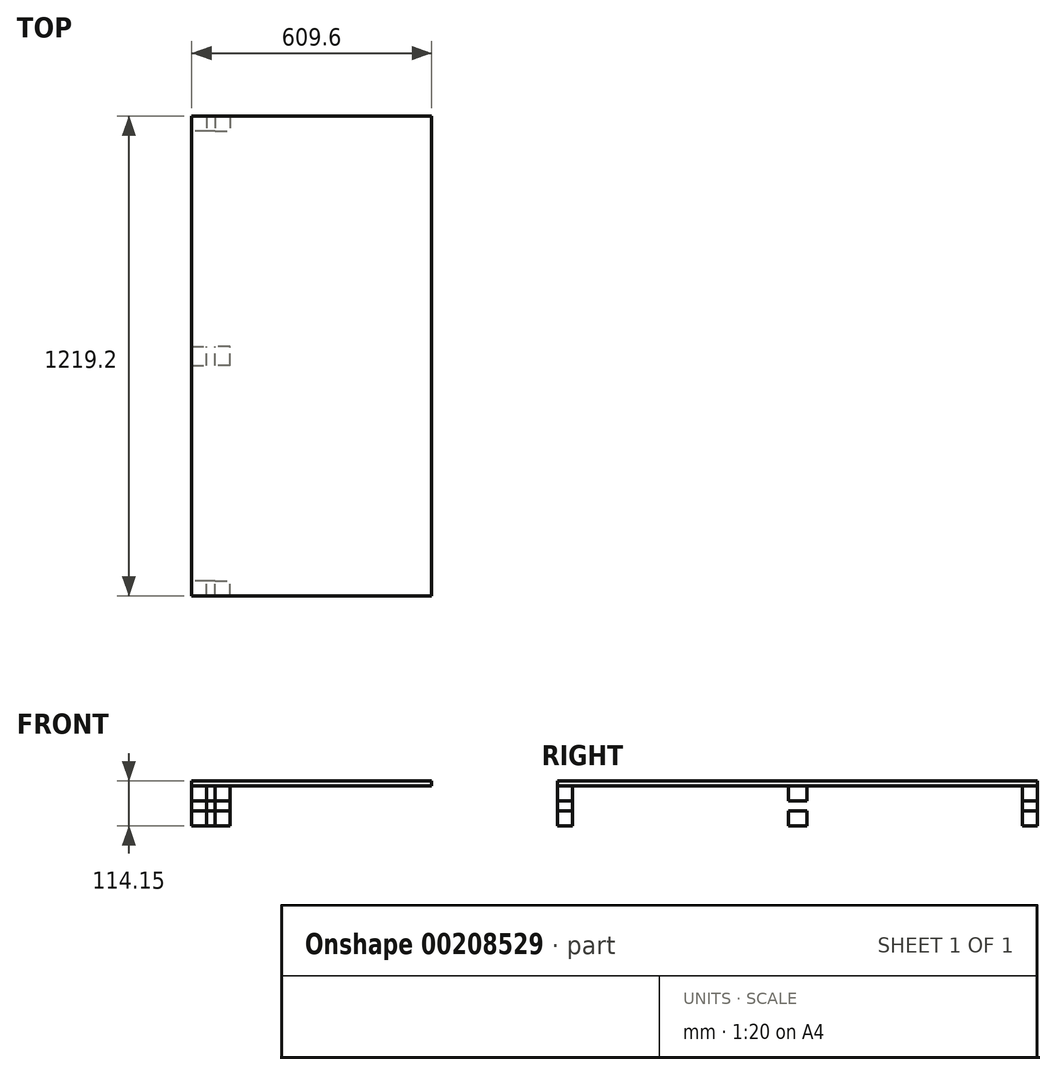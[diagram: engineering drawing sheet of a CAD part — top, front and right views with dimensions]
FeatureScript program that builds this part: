
annotation { "Feature Type Name" : "Feature", "Feature Type Description" : "" }
export const myFeature = defineFeature(function(context is Context, id is Id, definition is map)
    precondition{}
    {
        {
            assignVariable(context, id + "F0", {"name" : "ExtrudeSize", "anyValue" : 1});
        }
        {
            assignVariable(context, id + "F1", {"name" : "ProfileWidth", "anyValue" : [1, 1.5, 1.5][getVariable(context, 'ExtrudeSize')]});
        }
        {
            assignVariable(context, id + "F2", {"name" : "ProfileHeight", "anyValue" : [1, 1.5, 3][getVariable(context, 'ExtrudeSize')]});
        }
        {
            assignVariable(context, id + "F3", {"name" : "Length", "anyValue" : 48});
        }
        {
            assignVariable(context, id + "F4", {"name" : "Width", "anyValue" : 24});
        }
        {
            assignVariable(context, id + "F5", {"name" : "Height", "anyValue" : 34});
        }
        {
            assignVariable(context, id + "F6", {"name" : "AcrylicThickness", "anyValue" : .5});
        }
        {
            var Q0;
            Q0=qCreatedBy(makeId("Front.planeOp"),FACE);
            var sketch = newSketch(context, id + "F7", { "sketchPlane" : qUnion([Q0])});
            skLineSegment(sketch, "E0.bottom", {"start": v(0, 0) * mm, "end": v(38.1, 0) * mm});
            skLineSegment(sketch, "E0.top", {"start": v(0, 38.1) * mm, "end": v(38.1, 38.1) * mm});
            skLineSegment(sketch, "E0.left", {"start": v(0, 0) * mm, "end": v(0, 38.1) * mm});
            skLineSegment(sketch, "E0.right", {"start": v(38.1, 0) * mm, "end": v(38.1, 38.1) * mm});
            skSolve(sketch);
        }
        {
            var Q0;
            Q0 = qSketchRegion(id + "F7", true);
            extrude(context, id + "F8", {"entities" : qUnion([Q0]), "depth" : (getVariable(context, 'Length')) * mm, "symmetric" : true});
        }
        {
            var Q0;
            Q0=makeQuery(id+"F8.opExtrude","SWEPT_FACE",FACE,{"disambiguationData":[OSD([sQuery(id+"F7.wireOp",EDGE,"E0.right")])]});
            var sketch = newSketch(context, id + "F9", { "sketchPlane" : qUnion([Q0])});
            skLineSegment(sketch, "E1.bottom", {"start": v(-609.6, 0) * mm, "end": v(-571.5, 0) * mm});
            skLineSegment(sketch, "E1.top", {"start": v(-609.6, 38.1) * mm, "end": v(-571.5, 38.1) * mm});
            skLineSegment(sketch, "E1.left", {"start": v(-609.6, 0) * mm, "end": v(-609.6, 38.1) * mm});
            skLineSegment(sketch, "E1.right", {"start": v(-571.5, 0) * mm, "end": v(-571.5, 38.1) * mm});
            skSolve(sketch);
        }
        {
            var Q0;
            Q0=makeQuery(id+"F9.imprint","IMPRINT",FACE,{"disambiguationData":[TD([[makeQuery(id+"F9.imprint","IMPRINT",EDGE,{"derivedFrom":sQuery(id+"F9.wireOp",EDGE,"E1.bottom")}),1.0]])]});
            extrude(context, id + "F10", {"entities" : qUnion([Q0]), "depth" : ((getVariable(context, 'Width')) - 2 * (getVariable(context, 'ProfileWidth'))) * mm});
        }
        {
            var Q0;
            Q0=makeQuery(id+"F10.opExtrude","SWEPT_BODY",BODY,{"disambiguationData":[OSD([sQuery(id+"F9.wireOp",EDGE,"E1.bottom"),sQuery(id+"F9.wireOp",EDGE,"E1.top"),sQuery(id+"F9.wireOp",EDGE,"E1.left"),sQuery(id+"F9.wireOp",EDGE,"E1.right")])]});
            var Q1;
            Q1=qCreatedBy(makeId("Front.planeOp"),FACE);
            mirror(context, id + "F11", {"entities" : qUnion([Q0]), "mirrorPlane" : qUnion([Q1])});
        }
        {
            var Q0;
            Q0=makeQuery(id+"F10.opExtrude","CAP_FACE",FACE,{"disambiguationData":[OSD([sQuery(id+"F9.wireOp",EDGE,"E1.bottom"),sQuery(id+"F9.wireOp",EDGE,"E1.top"),sQuery(id+"F9.wireOp",EDGE,"E1.left"),sQuery(id+"F9.wireOp",EDGE,"E1.right")])],"isStart":false});
            var Q1;
            Q1=makeQuery(id+"F10.opExtrude","CAP_FACE",FACE,{"disambiguationData":[OSD([sQuery(id+"F9.wireOp",EDGE,"E1.bottom"),sQuery(id+"F9.wireOp",EDGE,"E1.top"),sQuery(id+"F9.wireOp",EDGE,"E1.left"),sQuery(id+"F9.wireOp",EDGE,"E1.right")])],"isStart":true});
            cPlane(context, id + "F12", {"entities" : qUnion([Q0, Q1]), "cplaneType" : CPlaneType.MID_PLANE, "offset" : 25.4 * mm, "width" : 152.4 * mm, "height" : 152.4 * mm});
        }
        {
            var Q0;
            Q0=makeQuery(id+"F8.opExtrude","SWEPT_BODY",BODY,{"disambiguationData":[OSD([sQuery(id+"F7.wireOp",EDGE,"E0.bottom"),sQuery(id+"F7.wireOp",EDGE,"E0.top"),sQuery(id+"F7.wireOp",EDGE,"E0.left"),sQuery(id+"F7.wireOp",EDGE,"E0.right")])]});
            var Q1;
            Q1=qCreatedBy(id+"F12.planeOp",FACE);
            mirror(context, id + "F13", {"entities" : qUnion([Q0]), "mirrorPlane" : qUnion([Q1])});
        }
        {
            var Q0;
            Q0=makeQuery(id+"F8.opExtrude","SWEPT_FACE",FACE,{"disambiguationData":[OSD([sQuery(id+"F7.wireOp",EDGE,"E0.top")])]});
            var sketch = newSketch(context, id + "F14", { "sketchPlane" : qUnion([Q0])});
            skLineSegment(sketch, "E2.bottom", {"start": v(38.1, -609.6) * mm, "end": v(0, -609.6) * mm});
            skLineSegment(sketch, "E2.top", {"start": v(38.1, -571.5) * mm, "end": v(0, -571.5) * mm});
            skLineSegment(sketch, "E2.left", {"start": v(38.1, -609.6) * mm, "end": v(38.1, -571.5) * mm});
            skLineSegment(sketch, "E2.right", {"start": v(0, -609.6) * mm, "end": v(0, -571.5) * mm});
            skSolve(sketch);
        }
        {
            var Q0;
            Q0 = qSketchRegion(id + "F14", true);
            extrude(context, id + "F15", {"entities" : qUnion([Q0]), "depth" : (getVariable(context, 'Height') - ((2 * (getVariable(context, 'ProfileHeight'))) + 5.25 + (getVariable(context, 'AcrylicThickness')))) * mm});
        }
        {
            var Q0;
            Q0=makeQuery(id+"F15.opExtrude","SWEPT_BODY",BODY,{"disambiguationData":[OSD([sQuery(id+"F14.wireOp",EDGE,"E2.bottom"),sQuery(id+"F14.wireOp",EDGE,"E2.top"),sQuery(id+"F14.wireOp",EDGE,"E2.left"),sQuery(id+"F14.wireOp",EDGE,"E2.right")])]});
            var Q1;
            Q1=qCreatedBy(makeId("Front.planeOp"),FACE);
            mirror(context, id + "F16", {"entities" : qUnion([Q0]), "mirrorPlane" : qUnion([Q1])});
        }
        {
            var Q0;
            Q0=makeQuery(id+"F15.opExtrude","SWEPT_BODY",BODY,{"disambiguationData":[OSD([sQuery(id+"F14.wireOp",EDGE,"E2.bottom"),sQuery(id+"F14.wireOp",EDGE,"E2.top"),sQuery(id+"F14.wireOp",EDGE,"E2.left"),sQuery(id+"F14.wireOp",EDGE,"E2.right")])]});
            var Q1;
            Q1=makeQuery(id+"F16.opPattern","COPY",BODY,{"derivedFrom":makeQuery(id+"F15.opExtrude","SWEPT_BODY",BODY,{"disambiguationData":[OSD([sQuery(id+"F14.wireOp",EDGE,"E2.bottom"),sQuery(id+"F14.wireOp",EDGE,"E2.top"),sQuery(id+"F14.wireOp",EDGE,"E2.left"),sQuery(id+"F14.wireOp",EDGE,"E2.right")])]}),"instanceName":"1"});
            var Q2;
            Q2=qCreatedBy(id+"F12.planeOp",FACE);
            mirror(context, id + "F17", {"entities" : qUnion([Q0, Q1]), "mirrorPlane" : qUnion([Q2])});
        }
        {
            var Q0;
            Q0=makeQuery(id+"F16.opPattern","COPY",FACE,{"derivedFrom":makeQuery(id+"F15.opExtrude","CAP_FACE",FACE,{"disambiguationData":[OSD([sQuery(id+"F14.wireOp",EDGE,"E2.bottom"),sQuery(id+"F14.wireOp",EDGE,"E2.top"),sQuery(id+"F14.wireOp",EDGE,"E2.left"),sQuery(id+"F14.wireOp",EDGE,"E2.right")])],"isStart":false}),"instanceName":"1"});
            var Q1;
            Q1=makeQuery(id+"F16.opPattern","COPY",FACE,{"derivedFrom":makeQuery(id+"F15.opExtrude","CAP_FACE",FACE,{"disambiguationData":[OSD([sQuery(id+"F14.wireOp",EDGE,"E2.bottom"),sQuery(id+"F14.wireOp",EDGE,"E2.top"),sQuery(id+"F14.wireOp",EDGE,"E2.left"),sQuery(id+"F14.wireOp",EDGE,"E2.right")])],"isStart":true}),"instanceName":"1"});
            cPlane(context, id + "F18", {"entities" : qUnion([Q0, Q1]), "cplaneType" : CPlaneType.MID_PLANE, "offset" : 25.4 * mm, "width" : 152.4 * mm, "height" : 152.4 * mm});
        }
        {
            var Q0;
            Q0=makeQuery(id+"F8.opExtrude","SWEPT_BODY",BODY,{"disambiguationData":[OSD([sQuery(id+"F7.wireOp",EDGE,"E0.bottom"),sQuery(id+"F7.wireOp",EDGE,"E0.top"),sQuery(id+"F7.wireOp",EDGE,"E0.left"),sQuery(id+"F7.wireOp",EDGE,"E0.right")])]});
            var Q1;
            Q1=makeQuery(id+"F11.opPattern","COPY",BODY,{"derivedFrom":makeQuery(id+"F10.opExtrude","SWEPT_BODY",BODY,{"disambiguationData":[OSD([sQuery(id+"F9.wireOp",EDGE,"E1.bottom"),sQuery(id+"F9.wireOp",EDGE,"E1.top"),sQuery(id+"F9.wireOp",EDGE,"E1.left"),sQuery(id+"F9.wireOp",EDGE,"E1.right")])]}),"instanceName":"1"});
            var Q2;
            Q2=makeQuery(id+"F13.opPattern","COPY",BODY,{"derivedFrom":makeQuery(id+"F8.opExtrude","SWEPT_BODY",BODY,{"disambiguationData":[OSD([sQuery(id+"F7.wireOp",EDGE,"E0.bottom"),sQuery(id+"F7.wireOp",EDGE,"E0.top"),sQuery(id+"F7.wireOp",EDGE,"E0.left"),sQuery(id+"F7.wireOp",EDGE,"E0.right")])]}),"instanceName":"1"});
            var Q3;
            Q3=makeQuery(id+"F10.opExtrude","SWEPT_BODY",BODY,{"disambiguationData":[OSD([sQuery(id+"F9.wireOp",EDGE,"E1.bottom"),sQuery(id+"F9.wireOp",EDGE,"E1.top"),sQuery(id+"F9.wireOp",EDGE,"E1.left"),sQuery(id+"F9.wireOp",EDGE,"E1.right")])]});
            var Q4;
            Q4=qCreatedBy(id+"F18.planeOp",FACE);
            mirror(context, id + "F19", {"entities" : qUnion([Q0, Q1, Q2, Q3]), "mirrorPlane" : qUnion([Q4])});
        }
        {
            var Q0;
            Q0=makeQuery(id+"F19.opPattern","COPY",FACE,{"derivedFrom":makeQuery(id+"F8.opExtrude","SWEPT_FACE",FACE,{"disambiguationData":[OSD([sQuery(id+"F7.wireOp",EDGE,"E0.bottom")])]}),"instanceName":"1"});
            var sketch = newSketch(context, id + "F20", { "sketchPlane" : qUnion([Q0])});
            skLineSegment(sketch, "E3.bottom", {"start": v(0, 609.6) * mm, "end": v(609.6, 609.6) * mm});
            skLineSegment(sketch, "E3.top", {"start": v(0, -609.6) * mm, "end": v(609.6, -609.6) * mm});
            skLineSegment(sketch, "E3.left", {"start": v(0, 609.6) * mm, "end": v(0, -609.6) * mm});
            skLineSegment(sketch, "E3.right", {"start": v(609.6, 609.6) * mm, "end": v(609.6, -609.6) * mm});
            skSolve(sketch);
        }
        {
            var Q0;
            Q0 = qSketchRegion(id + "F20", true);
            extrude(context, id + "F21", {"entities" : qUnion([Q0]), "depth" : 12.7 * mm});
        }
    });
